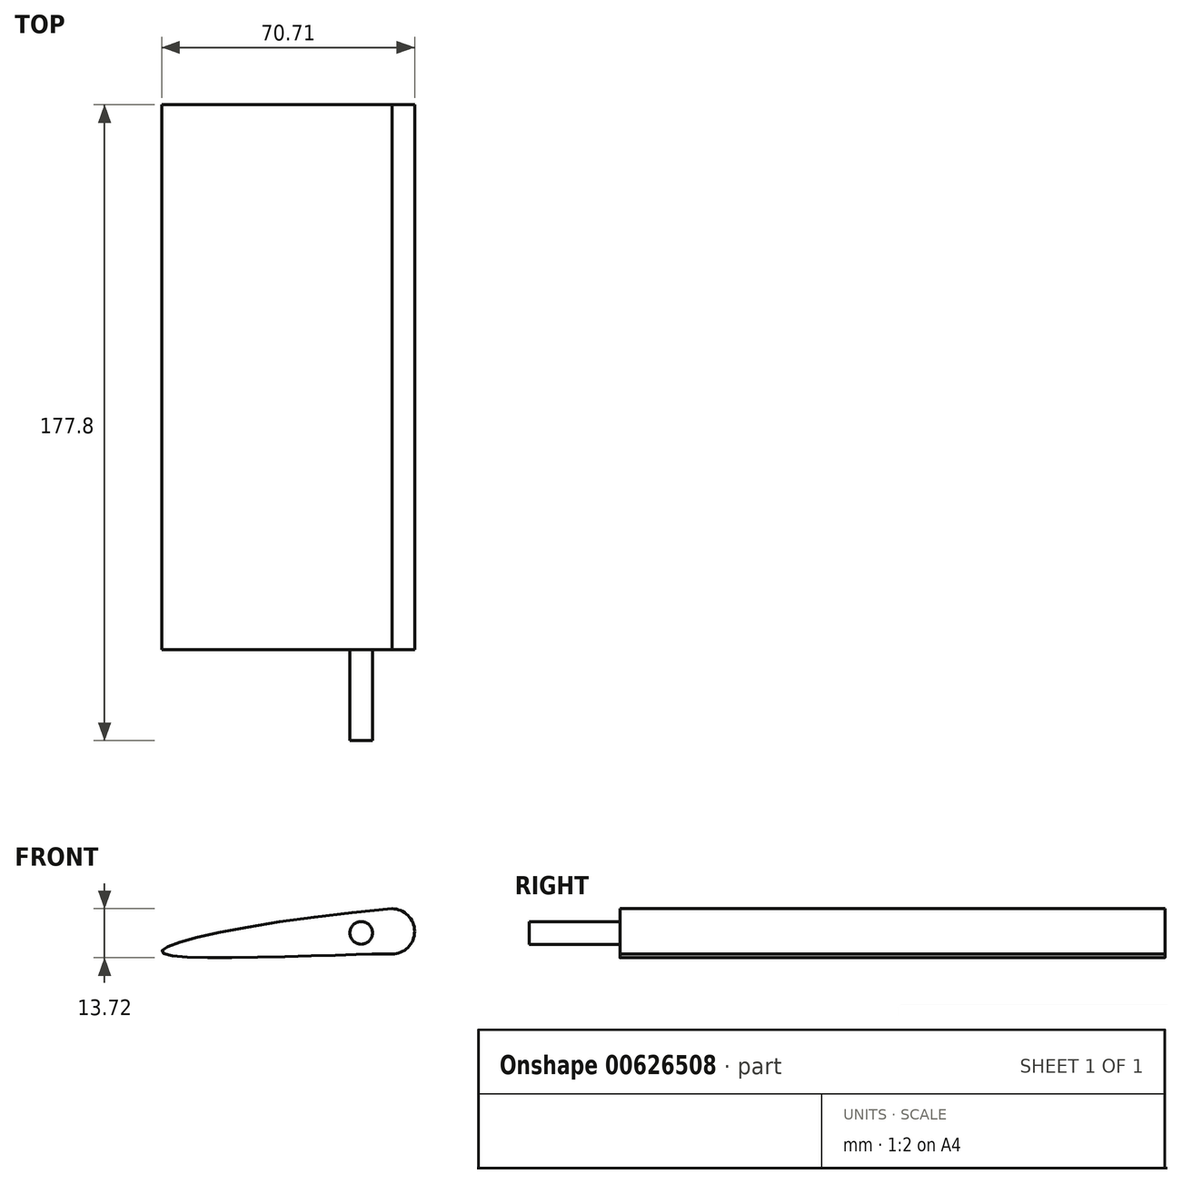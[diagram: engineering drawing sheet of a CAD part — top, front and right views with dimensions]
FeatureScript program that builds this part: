
annotation { "Feature Type Name" : "Feature", "Feature Type Description" : "" }
export const myFeature = defineFeature(function(context is Context, id is Id, definition is map)
    precondition{}
    {
        {
            var Q0;
            Q0=qCreatedBy(makeId("Front.planeOp"),FACE);
            var sketch = newSketch(context, id + "F0", { "sketchPlane" : qUnion([Q0])});
            skArc(sketch, "E0", {"start": v(63.5, 0) * mm, "mid": v(69.85, 6.35) * mm, "end": v(63.5, 12.7) * mm});
            skFitSpline(sketch, "E1", {"points": [v(63.5, 0) * mm, v(57.58, 0) * mm, v(0, 0) * mm, v(63.5, 12.7) * mm], "startDerivative": vector(-22.39, -1.19) * mm, "endDerivative": vector(262.51, 22.6) * mm});
            skLineSegment(sketch, "E2", {"start": v(63.5, 12.7) * mm, "end": v(63.5, 0) * mm});
            skSolve(sketch);
        }
        {
            var Q0;
            Q0=makeQuery(id+"F0.imprint","IMPRINT",FACE,{"disambiguationData":[TD([[makeQuery(id+"F0.imprint","IMPRINT",EDGE,{"derivedFrom":sQuery(id+"F0.wireOp",EDGE,"E0")}),1.0]])]});
            var Q1;
            Q1=makeQuery(id+"F0.imprint","IMPRINT",FACE,{"disambiguationData":[TD([[makeQuery(id+"F0.imprint","IMPRINT",EDGE,{"derivedFrom":sQuery(id+"F0.wireOp",EDGE,"E1")}),-1.0]])]});
            extrude(context, id + "F1", {"entities" : qUnion([Q0, Q1]), "depth" : 152.4 * mm, "offsetDistance" : 25.4 * mm});
        }
        {
            var Q0;
            Q0=makeQuery(id+"F1.opExtrude","CAP_FACE",FACE,{"disambiguationData":[OSD([sQuery(id+"F0.wireOp",EDGE,"E0"),sQuery(id+"F0.wireOp",EDGE,"E1")])],"isStart":false});
            var sketch = newSketch(context, id + "F2", { "sketchPlane" : qUnion([Q0])});
            skCircle(sketch, "E3", {"center": v(54.91, 5.95) * mm, "radius": 3.18 * mm});
            skSolve(sketch);
        }
        {
            var Q0;
            Q0=makeQuery(id+"F2.imprint","IMPRINT",FACE,{"disambiguationData":[TD([[makeQuery(id+"F2.imprint","IMPRINT",EDGE,{"derivedFrom":sQuery(id+"F2.wireOp",EDGE,"E3")}),1.0]])]});
            extrude(context, id + "F3", {"entities" : qUnion([Q0]), "operationType" : NewBodyOperationType.ADD, "depth" : 25.4 * mm, "offsetDistance" : 25.4 * mm});
        }
    });
